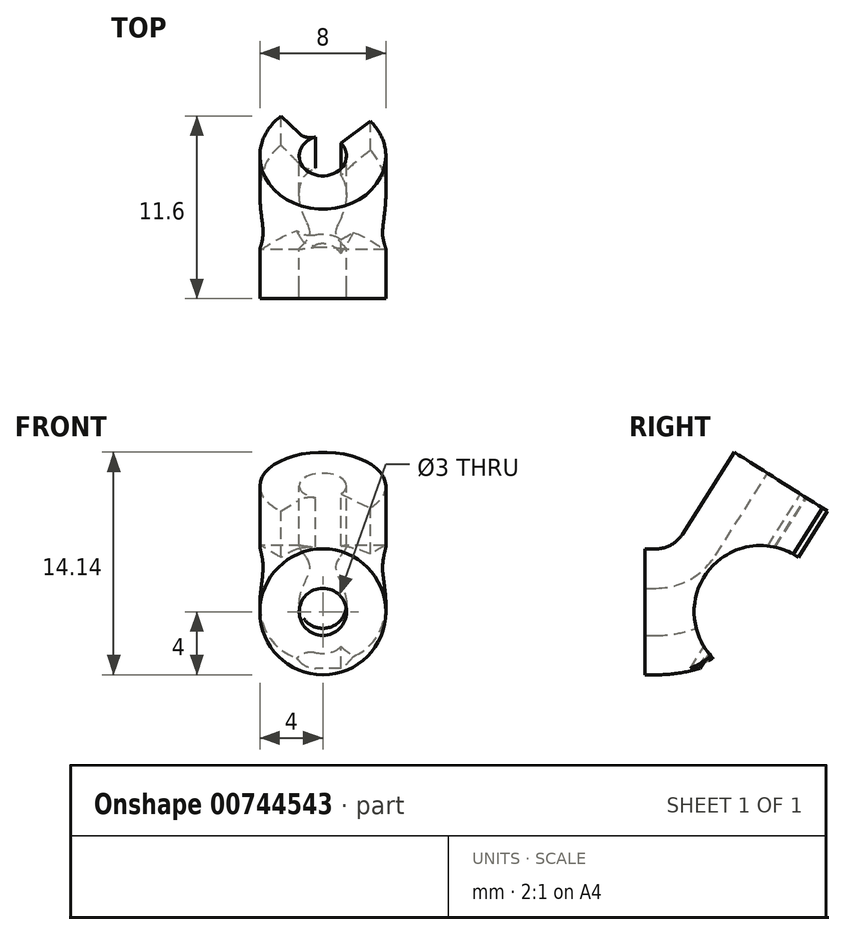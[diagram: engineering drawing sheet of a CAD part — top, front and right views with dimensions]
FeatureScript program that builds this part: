
annotation { "Feature Type Name" : "Feature", "Feature Type Description" : "" }
export const myFeature = defineFeature(function(context is Context, id is Id, definition is map)
    precondition{}
    {
        {
            var Q0;
            Q0=qCreatedBy(makeId("Front.planeOp"),FACE);
            var sketch = newSketch(context, id + "F0", { "sketchPlane" : qUnion([Q0])});
            skCircle(sketch, "E0", {"center": v(0, 0) * mm, "radius": 1.5 * mm});
            skCircle(sketch, "E1", {"center": v(0, 0) * mm, "radius": 4 * mm});
            skSolve(sketch);
        }
        {
            var Q0;
            Q0=qCreatedBy(makeId("Right.planeOp"),FACE);
            var sketch = newSketch(context, id + "F1", { "sketchPlane" : qUnion([Q0])});
            skLineSegment(sketch, "E2", {"start": v(0, 0) * mm, "end": v(0.7, 0) * mm});
            skLineSegment(sketch, "E3", {"start": v(5.77, 2.79) * mm, "end": v(9.07, 8) * mm});
            skPoint(sketch, "E4.visualSharp", {"position": v(4, 0) * mm});
            skArc(sketch, "E4.filletArc", {"start": v(0.7, 0) * mm, "mid": v(3.6, 0.74) * mm, "end": v(5.77, 2.79) * mm});
            skSolve(sketch);
        }
        {
            var Q0;
            Q0=makeQuery(id+"F0.imprint","IMPRINT",FACE,{"disambiguationData":[TD([[makeQuery(id+"F0.imprint","IMPRINT",EDGE,{"derivedFrom":sQuery(id+"F0.wireOp",EDGE,"E0")}),-1.0]])]});
            var Q1;
            Q1=sQuery(id+"F1.wireOp",EDGE,"E2");
            var Q2;
            Q2=sQuery(id+"F1.wireOp",EDGE,"E4.filletArc");
            var Q3;
            Q3=sQuery(id+"F1.wireOp",EDGE,"E3");
            sweep(context, id + "F2", {"profiles" : qUnion([Q0]), "path" : qUnion([Q1, Q2, Q3])});
        }
        {
            var Q0;
            Q0=makeQuery(id+"F2.opSweep","CAP_FACE",FACE,{"disambiguationData":[OSD([sQuery(id+"F0.wireOp",EDGE,"E0"),sQuery(id+"F0.wireOp",EDGE,"E1"),sQuery(id+"F1.wireOp",VERTEX,"E3.end")])],"isStart":false});
            var sketch = newSketch(context, id + "F3", { "sketchPlane" : qUnion([Q0])});
            skLineSegment(sketch, "E5.0", {"start": v(4.73, 7.5) * mm, "end": v(-3.45, 7.29) * mm});
            skLineSegment(sketch, "E5.1", {"start": v(0, 3.36) * mm, "end": v(4.73, 7.5) * mm});
            skLineSegment(sketch, "E5.2", {"start": v(-3.45, 7.29) * mm, "end": v(0, 3.36) * mm});
            skPoint(sketch, "E5.0.midPoint", {"position": v(0.64, 7.4) * mm});
            skSolve(sketch);
        }
        {
            var Q0;
            {var subQ0=sQuery(id+"F3.wireOp",EDGE,"E5.1");var subQ1=sQuery(id+"F1.wireOp",VERTEX,"E3.end");var subQ6=makeQuery(id+"F2.opSweep","CAP_EDGE",EDGE,{"disambiguationData":[OSD([sQuery(id+"F0.wireOp",EDGE,"E1"),subQ1])],"isStart":false});var subQ8=makeQuery(id+"F3.imprint","INTERSECT",VERTEX,{"derivedFrom":[subQ6,subQ0]});Q0=makeQuery(id+"F3.imprint","IMPRINT",FACE,{"disambiguationData":[TD([[makeQuery(id+"F3.imprint","IMPRINT",EDGE,{"disambiguationData":[TD([[subQ8,1.0]])],"derivedFrom":subQ0}),1.0]])]});}
            var Q1;
            {var subQ0=sQuery(id+"F3.wireOp",EDGE,"E5.1");var subQ1=sQuery(id+"F3.wireOp",EDGE,"E5.0");var subQ2=makeQuery(id+"F3.imprint","INTERSECT",VERTEX,{"derivedFrom":[subQ1,subQ0]});Q1=makeQuery(id+"F3.imprint","IMPRINT",FACE,{"disambiguationData":[TD([[makeQuery(id+"F3.imprint","IMPRINT",EDGE,{"disambiguationData":[TD([[subQ2,-1.0]])],"derivedFrom":subQ1}),1.0]])]});}
            var Q2;
            {var subQ0=sQuery(id+"F3.wireOp",EDGE,"E5.2");var subQ1=sQuery(id+"F3.wireOp",EDGE,"E5.0");var subQ2=makeQuery(id+"F3.imprint","INTERSECT",VERTEX,{"derivedFrom":[subQ1,subQ0]});Q2=makeQuery(id+"F3.imprint","IMPRINT",FACE,{"disambiguationData":[TD([[makeQuery(id+"F3.imprint","IMPRINT",EDGE,{"disambiguationData":[TD([[subQ2,1.0]])],"derivedFrom":subQ1}),1.0]])]});}
            extrude(context, id + "F4", {"entities" : qUnion([Q0, Q1, Q2]), "operationType" : NewBodyOperationType.REMOVE, "endBound" : BoundingType.THROUGH_ALL, "oppositeDirection" : true, "depth" : 25.4 * mm, "offsetDistance" : 25.4 * mm});
        }
        {
            var Q0;
            {var subQ0=sQuery(id+"F0.wireOp",EDGE,"E0");var subQ1=sQuery(id+"F3.wireOp",EDGE,"E5.2");Q0=makeQuery(id+"F4.boolean.opBoolean","COPY",EDGE,{"disambiguationData":[topologyDisambiguationEdgeConnected([makeQuery(id+"F2.opSweep","SWEPT_FACE",FACE,{"disambiguationData":[OSD([subQ0,sQuery(id+"F1.wireOp",EDGE,"E3")])]})])],"derivedFrom":makeQuery(id+"F4.opExtrude","SWEPT_EDGE",EDGE,{"disambiguationData":[OSD([subQ0,sQuery(id+"F1.wireOp",VERTEX,"E3.end"),subQ1])]})});}
            fillet(context, id + "F5", {"entities" : qUnion([Q0]), "radius" : 1 * mm, "tangentPropagation" : true, "allowEdgeOverflow" : false});
        }
        {
            var Q0;
            Q0=qCreatedBy(makeId("Right.planeOp"),FACE);
            var sketch = newSketch(context, id + "F6", { "sketchPlane" : qUnion([Q0])});
            skCircle(sketch, "E6", {"center": v(7.34, 0) * mm, "radius": 4.21 * mm});
            skSolve(sketch);
        }
        {
            var Q0;
            Q0=makeQuery(id+"F6.imprint","IMPRINT",FACE,{"disambiguationData":[TD([[makeQuery(id+"F6.imprint","IMPRINT",EDGE,{"derivedFrom":sQuery(id+"F6.wireOp",EDGE,"E6")}),1.0]])]});
            extrude(context, id + "F7", {"entities" : qUnion([Q0]), "operationType" : NewBodyOperationType.REMOVE, "endBound" : BoundingType.SYMMETRIC, "depth" : 25.4 * mm, "offsetDistance" : 25.4 * mm});
        }
    });
